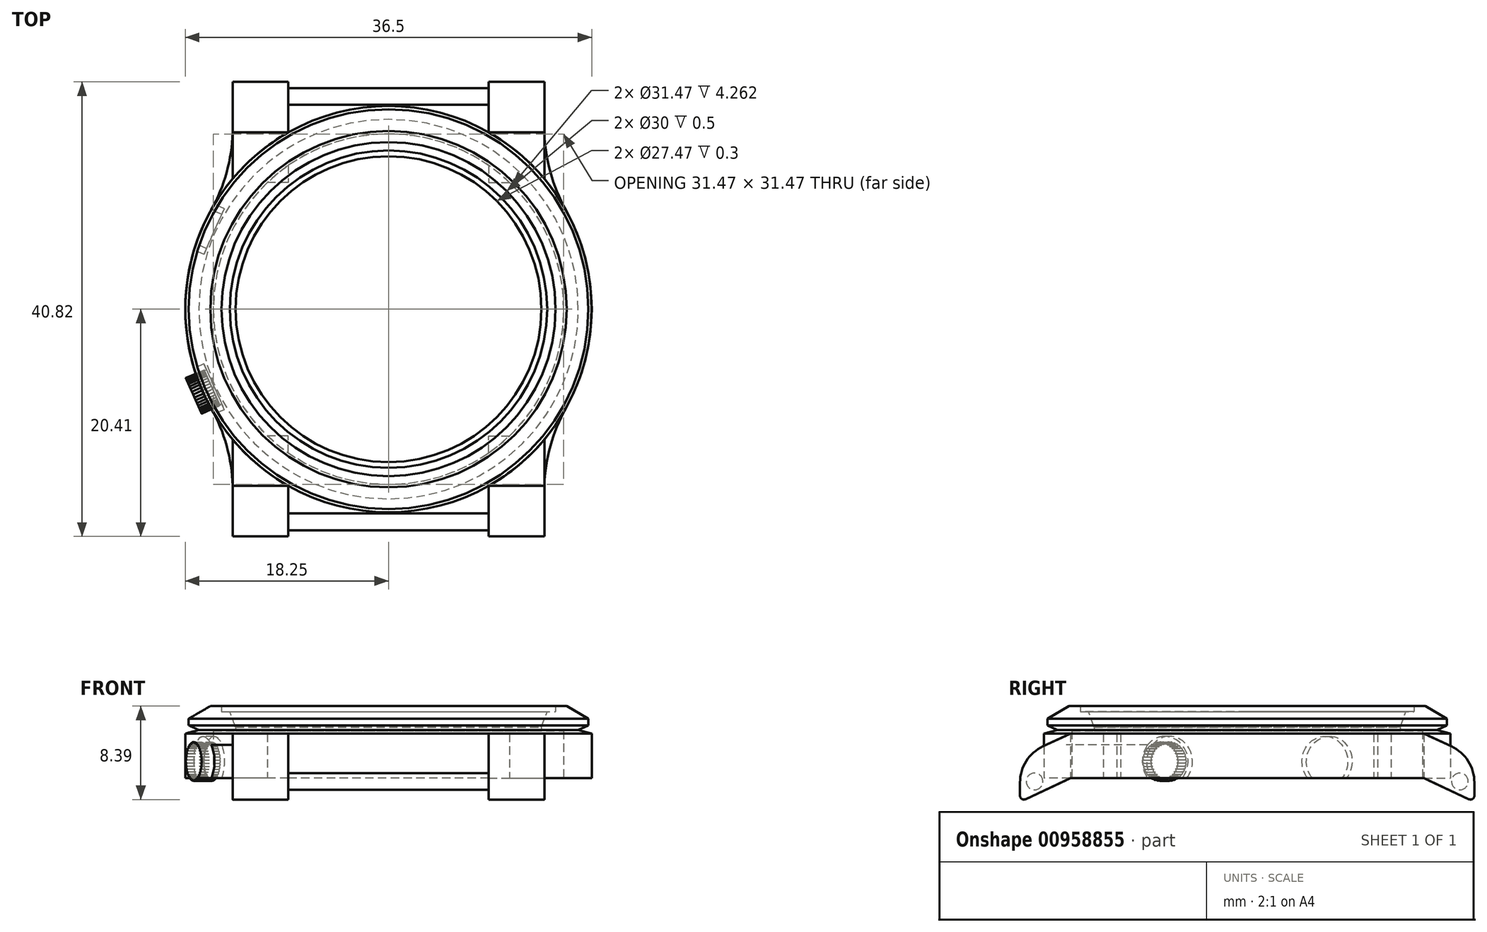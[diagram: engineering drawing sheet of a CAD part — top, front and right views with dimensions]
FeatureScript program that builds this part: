
annotation { "Feature Type Name" : "Feature", "Feature Type Description" : "" }
export const myFeature = defineFeature(function(context is Context, id is Id, definition is map)
    precondition{}
    {
        {
            var Q0;
            Q0=qCreatedBy(makeId("Right.planeOp"),FACE);
            var sketch = newSketch(context, id + "F0", { "sketchPlane" : qUnion([Q0])});
            skLineSegment(sketch, "E0", {"start": v(0, 0) * mm, "end": v(18.25, 0) * mm});
            skLineSegment(sketch, "E1", {"start": v(18.25, 0) * mm, "end": v(18.25, 4) * mm});
            skLineSegment(sketch, "E2", {"start": v(18.25, 4) * mm, "end": v(17.04, 4.32) * mm});
            skLineSegment(sketch, "E3", {"start": v(17.04, 4.32) * mm, "end": v(17.95, 4.75) * mm});
            skLineSegment(sketch, "E4", {"start": v(17.95, 4.75) * mm, "end": v(17.95, 5.35) * mm});
            skLineSegment(sketch, "E5", {"start": v(17.95, 5.35) * mm, "end": v(16, 6.47) * mm});
            skLineSegment(sketch, "E6", {"start": v(15, 5.97) * mm, "end": v(14.25, 5.97) * mm});
            skLineSegment(sketch, "E7", {"start": v(14.25, 5.97) * mm, "end": v(13.74, 4.56) * mm});
            skLineSegment(sketch, "E8", {"start": v(13.74, 4.56) * mm, "end": v(13.74, 4.26) * mm});
            skLineSegment(sketch, "E9", {"start": v(0, 0) * mm, "end": v(0, 9.09) * mm, "construction": true});
            skLineSegment(sketch, "E10", {"start": v(16, 6.47) * mm, "end": v(15, 6.47) * mm});
            skLineSegment(sketch, "E11", {"start": v(15, 6.47) * mm, "end": v(15, 5.97) * mm});
            skLineSegment(sketch, "E12", {"start": v(13.74, 4.26) * mm, "end": v(15.74, 4.26) * mm});
            skLineSegment(sketch, "E13", {"start": v(15.74, 4.26) * mm, "end": v(15.74, 0) * mm});
            skSolve(sketch);
        }
        {
            var Q0;
            Q0=qSketchRegion(id+"F0",true);
            var Q1;
            Q1=sQuery(id+"F0.wireOp",EDGE,"E9");
            revolve(context, id + "F1", {"entities" : qUnion([Q0]), "axis" : qUnion([Q1]), "revolveType" : RevolveType.FULL});
        }
        {
            var Q0;
            Q0=makeQuery(id+"F1.opRevolve","SWEPT_FACE",FACE,{"disambiguationData":[OSD([sQuery(id+"F0.wireOp",EDGE,"E0")])]});
            var sketch = newSketch(context, id + "F2", { "sketchPlane" : qUnion([Q0])});
            skLineSegment(sketch, "E14", {"start": v(-9, -15.88) * mm, "end": v(9, -15.88) * mm});
            skSolve(sketch);
        }
        {
            var Q0;
            Q0=qCreatedBy(makeId("Front.planeOp"),FACE);
            var Q1;
            Q1=sQuery(id+"F2.wireOp",VERTEX,"E14.start");
            cPlane(context, id + "F3", {"entities" : qUnion([Q0, Q1]), "cplaneType" : CPlaneType.PLANE_POINT, "offset" : 150 * mm, "width" : 150 * mm, "height" : 150 * mm});
        }
        {
            var Q0;
            Q0=qCreatedBy(id+"F3.planeOp",FACE);
            var sketch = newSketch(context, id + "F4", { "sketchPlane" : qUnion([Q0])});
            skLineSegment(sketch, "E15.bottom", {"start": v(-9, 0) * mm, "end": v(-14, 0) * mm});
            skLineSegment(sketch, "E15.top", {"start": v(-9, 4) * mm, "end": v(-14, 4) * mm});
            skLineSegment(sketch, "E15.left", {"start": v(-9, 0) * mm, "end": v(-9, 4) * mm});
            skLineSegment(sketch, "E15.right", {"start": v(-14, 0) * mm, "end": v(-14, 4) * mm});
            skSolve(sketch);
        }
        {
            var Q0;
            Q0=qCreatedBy(makeId("Top.planeOp"),FACE);
            var sketch = newSketch(context, id + "F5", { "sketchPlane" : qUnion([Q0])});
            skLineSegment(sketch, "E16", {"start": v(-11.51, 15.88) * mm, "end": v(-11.51, 11.38) * mm});
            skSolve(sketch);
        }
        {
            var Q0;
            Q0=sQuery(id+"F4.wireOp",EDGE,"E15.bottom");
            cPlane(context, id + "F6", {"entities" : qUnion([Q0]), "cplaneType" : CPlaneType.LINE_ANGLE, "offset" : 150 * mm, "angle" : 115 * degree, "width" : 150 * mm, "height" : 150 * mm});
        }
        {
            var Q0;
            Q0=qCreatedBy(id+"F6.planeOp",FACE);
            var sketch = newSketch(context, id + "F7", { "sketchPlane" : qUnion([Q0])});
            skLineSegment(sketch, "E17", {"start": v(-11.51, 14.39) * mm, "end": v(-11.51, 19.39) * mm});
            skSolve(sketch);
        }
        {
            var Q0;
            Q0=qSketchRegion(id+"F4",true);
            var Q1;
            Q1=sQuery(id+"F7.wireOp",EDGE,"E17");
            sweep(context, id + "F8", {"profiles" : qUnion([Q0]), "path" : qUnion([Q1])});
        }
        {
            var Q0;
            Q0=qSketchRegion(id+"F4",true);
            var Q1;
            Q1=qConstructionFilter(qBodyType(qCreatedBy(id+"F5",EDGE),BodyType.WIRE),ConstructionObject.NO);
            var Q2;
            Q2=qConstructionFilter(qBodyType(qCreatedBy(id+"F5",EDGE),BodyType.WIRE),ConstructionObject.NO);
            sweep(context, id + "F9", {"profiles" : qUnion([Q0]), "path" : qUnion([Q1, Q2])});
        }
        {
            var Q0;
            Q0=makeQuery(id+"F8.opSweep","CAP_EDGE",EDGE,{"disambiguationData":[OSD([sQuery(id+"F4.wireOp",EDGE,"E15.top"),sQuery(id+"F7.wireOp",VERTEX,"E17.end")])],"isStart":false});
            fillet(context, id + "F10", {"entities" : qUnion([Q0]), "radius" : 3.59 * mm, "tangentPropagation" : true, "allowEdgeOverflow" : false});
        }
        {
            var Q0;
            Q0=makeQuery(id+"F8.opSweep","CAP_EDGE",EDGE,{"disambiguationData":[OSD([sQuery(id+"F4.wireOp",EDGE,"E15.bottom"),sQuery(id+"F7.wireOp",VERTEX,"E17.end")])],"isStart":false});
            fillet(context, id + "F11", {"entities" : qUnion([Q0]), "radius" : 0.34 * mm, "tangentPropagation" : true, "allowEdgeOverflow" : false});
        }
        {
            var Q0;
            Q0=makeQuery(id+"F8.opSweep","SWEPT_BODY",BODY,{"disambiguationData":[OSD([sQuery(id+"F4.wireOp",EDGE,"E15.bottom"),sQuery(id+"F4.wireOp",EDGE,"E15.top"),sQuery(id+"F4.wireOp",EDGE,"E15.left"),sQuery(id+"F4.wireOp",EDGE,"E15.right"),sQuery(id+"F7.wireOp",EDGE,"E17")])]});
            var Q1;
            Q1=makeQuery(id+"F9.opSweep","SWEPT_BODY",BODY,{"disambiguationData":[OSD([sQuery(id+"F4.wireOp",EDGE,"E15.bottom"),sQuery(id+"F4.wireOp",EDGE,"E15.top"),sQuery(id+"F4.wireOp",EDGE,"E15.left"),sQuery(id+"F4.wireOp",EDGE,"E15.right"),sQuery(id+"F5.wireOp",EDGE,"E16")])]});
            var Q2;
            Q2=qCreatedBy(makeId("Right.planeOp"),FACE);
            mirror(context, id + "F12", {"entities" : qUnion([Q0, Q1]), "mirrorPlane" : qUnion([Q2])});
        }
        {
            var Q0;
            Q0=makeQuery(id+"F12.opPattern","COPY",BODY,{"derivedFrom":makeQuery(id+"F8.opSweep","SWEPT_BODY",BODY,{"disambiguationData":[OSD([sQuery(id+"F4.wireOp",EDGE,"E15.bottom"),sQuery(id+"F4.wireOp",EDGE,"E15.top"),sQuery(id+"F4.wireOp",EDGE,"E15.left"),sQuery(id+"F4.wireOp",EDGE,"E15.right"),sQuery(id+"F7.wireOp",EDGE,"E17")])]}),"instanceName":"1"});
            var Q1;
            Q1=makeQuery(id+"F12.opPattern","COPY",BODY,{"derivedFrom":makeQuery(id+"F9.opSweep","SWEPT_BODY",BODY,{"disambiguationData":[OSD([sQuery(id+"F4.wireOp",EDGE,"E15.bottom"),sQuery(id+"F4.wireOp",EDGE,"E15.top"),sQuery(id+"F4.wireOp",EDGE,"E15.left"),sQuery(id+"F4.wireOp",EDGE,"E15.right"),sQuery(id+"F5.wireOp",EDGE,"E16")])]}),"instanceName":"1"});
            var Q2;
            Q2=makeQuery(id+"F9.opSweep","SWEPT_BODY",BODY,{"disambiguationData":[OSD([sQuery(id+"F4.wireOp",EDGE,"E15.bottom"),sQuery(id+"F4.wireOp",EDGE,"E15.top"),sQuery(id+"F4.wireOp",EDGE,"E15.left"),sQuery(id+"F4.wireOp",EDGE,"E15.right"),sQuery(id+"F5.wireOp",EDGE,"E16")])]});
            var Q3;
            Q3=makeQuery(id+"F8.opSweep","SWEPT_BODY",BODY,{"disambiguationData":[OSD([sQuery(id+"F4.wireOp",EDGE,"E15.bottom"),sQuery(id+"F4.wireOp",EDGE,"E15.top"),sQuery(id+"F4.wireOp",EDGE,"E15.left"),sQuery(id+"F4.wireOp",EDGE,"E15.right"),sQuery(id+"F7.wireOp",EDGE,"E17")])]});
            var Q4;
            Q4=qCreatedBy(makeId("Front.planeOp"),FACE);
            mirror(context, id + "F13", {"operationType" : NewBodyOperationType.ADD, "entities" : qUnion([Q0, Q1, Q2, Q3]), "mirrorPlane" : qUnion([Q4])});
        }
        {
            var Q0;
            Q0=sQuery(id+"F0.wireOp",EDGE,"E9");
            cPlane(context, id + "F14", {"entities" : qUnion([Q0]), "cplaneType" : CPlaneType.LINE_ANGLE, "offset" : 150 * mm, "angle" : 114 * degree, "width" : 150 * mm, "height" : 150 * mm});
        }
        {
            var Q0;
            Q0=qCreatedBy(id+"F14.planeOp",FACE);
            var sketch = newSketch(context, id + "F15", { "sketchPlane" : qUnion([Q0])});
            skLineSegment(sketch, "E18", {"start": v(18.15, 4) * mm, "end": v(18.15, 0) * mm});
            skLineSegment(sketch, "E19", {"start": v(18.15, 4) * mm, "end": v(20.15, 4) * mm, "construction": true});
            skLineSegment(sketch, "E20", {"start": v(18.15, 1.5) * mm, "end": v(19.95, 1.5) * mm, "construction": true});
            skSolve(sketch);
        }
        {
            var Q0;
            Q0=sQuery(id+"F15.wireOp",EDGE,"E18");
            cPlane(context, id + "F16", {"entities" : qUnion([Q0]), "cplaneType" : CPlaneType.LINE_ANGLE, "offset" : 150 * mm, "angle" : 156 * degree, "width" : 150 * mm, "height" : 150 * mm});
        }
        {
            var Q0;
            Q0=qCreatedBy(id+"F16.planeOp",FACE);
            var sketch = newSketch(context, id + "F17", { "sketchPlane" : qUnion([Q0])});
            skCircle(sketch, "E21", {"center": v(0, 1.5) * mm, "radius": 2.25 * mm});
            skSolve(sketch);
        }
        {
            var Q0;
            Q0=qSketchRegion(id+"F17",true);
            extrude(context, id + "F18", {"entities" : qUnion([Q0]), "operationType" : NewBodyOperationType.REMOVE, "depth" : 1 * mm, "hasSecondDirection" : true, "secondDirectionBound" : SecondDirectionBoundingType.THROUGH_ALL, "secondDirectionOppositeDirection" : true, "secondDirectionDepth" : 25 * mm});
        }
        {
            var Q0;
            Q0=qCreatedBy(id+"F16.planeOp",FACE);
            var sketch = newSketch(context, id + "F19", { "sketchPlane" : qUnion([Q0])});
            skCircle(sketch, "E22", {"center": v(0, 1.5) * mm, "radius": 1.75 * mm});
            skSolve(sketch);
        }
        {
            var Q0;
            Q0=qSketchRegion(id+"F19",true);
            extrude(context, id + "F20", {"entities" : qUnion([Q0]), "depth" : .8 * mm, "hasSecondDirection" : true, "secondDirectionOppositeDirection" : true, "secondDirectionDepth" : 1 * mm});
        }
        {
            var Q0;
            Q0=qCreatedBy(id+"F16.planeOp",FACE);
            var sketch = newSketch(context, id + "F21", { "sketchPlane" : qUnion([Q0])});
            skCircle(sketch, "E23", {"center": v(0, -0.12) * mm, "radius": 0.12 * mm});
            skPoint(sketch, "E23.first.point", {"position": v(0, -0.25) * mm});
            skPoint(sketch, "E23.second.point", {"position": v(0, 0) * mm});
            skPoint(sketch, "E23.third.point", {"position": v(0.12, -0.15) * mm});
            skCircle(sketch, "E24", {"center": v(-0.25, -0.1) * mm, "radius": 0.12 * mm});
            skPoint(sketch, "E24.first.point", {"position": v(-0.27, -0.23) * mm});
            skPoint(sketch, "E24.second.point", {"position": v(-0.24, 0.02) * mm});
            skPoint(sketch, "E24.third.point", {"position": v(-0.3, 0) * mm});
            skLineSegment(sketch, "E25", {"start": v(0, -0.25) * mm, "end": v(-0.14, -0.32) * mm});
            skLineSegment(sketch, "E26", {"start": v(-0.14, -0.32) * mm, "end": v(-0.27, -0.23) * mm});
            skSolve(sketch);
        }
        {
            var Q0;
            {var subQ1=sQuery(id+"F21.wireOp",EDGE,"E25");Q0=makeQuery(id+"F21.imprint","IMPRINT",FACE,{"disambiguationData":[TD([[makeQuery(id+"F21.imprint","IMPRINT",EDGE,{"derivedFrom":subQ1}),-1.0]])]});}
            extrude(context, id + "F22", {"entities" : qUnion([Q0]), "endBound" : BoundingType.UP_TO_NEXT, "oppositeDirection" : true, "depth" : 25 * mm, "hasSecondDirection" : true, "secondDirectionBound" : SecondDirectionBoundingType.THROUGH_ALL, "secondDirectionOppositeDirection" : false, "secondDirectionDepth" : 25 * mm});
        }
        {
            var Q0;
            Q0=makeQuery(id+"F22.opExtrude","SWEPT_BODY",BODY,{"disambiguationData":[OSD([sQuery(id+"F21.wireOp",EDGE,"E23"),sQuery(id+"F21.wireOp",EDGE,"E24"),sQuery(id+"F21.wireOp",EDGE,"E25"),sQuery(id+"F21.wireOp",EDGE,"E26")])]});
            var Q1;
            Q1=sQuery(id+"F15.wireOp",EDGE,"E20");
            circularPattern(context, id + "F23", {"operationType" : NewBodyOperationType.REMOVE, "entities" : qUnion([Q0]), "axis" : qUnion([Q1]), "angle" : 10 * degree, "instanceCount" : 37});
        }
        {
            var Q0;
            {var subQ0=sQuery(id+"F4.wireOp",EDGE,"E15.left");Q0=makeQuery(id+"F13.boolean.opBoolean","MERGE",FACE,{"disambiguationData":[OD(1.0)],"derivedFrom":[makeQuery(id+"F12.opPattern","COPY",FACE,{"derivedFrom":makeQuery(id+"F9.opSweep","SWEPT_FACE",FACE,{"disambiguationData":[OSD([subQ0,sQuery(id+"F5.wireOp",EDGE,"E16")])]}),"instanceName":"1"}),makeQuery(id+"F12.opPattern","COPY",FACE,{"derivedFrom":makeQuery(id+"F8.opSweep","SWEPT_FACE",FACE,{"disambiguationData":[OSD([subQ0,sQuery(id+"F7.wireOp",EDGE,"E17")])]}),"instanceName":"1"})]});}
            var sketch = newSketch(context, id + "F24", { "sketchPlane" : qUnion([Q0])});
            skCircle(sketch, "E27", {"center": v(-19.1, -0.3) * mm, "radius": 0.75 * mm});
            skSolve(sketch);
        }
        {
            var Q0;
            Q0=qSketchRegion(id+"F24",true);
            extrude(context, id + "F25", {"entities" : qUnion([Q0]), "operationType" : NewBodyOperationType.ADD, "endBound" : BoundingType.UP_TO_NEXT, "depth" : 25 * mm});
        }
        {
            var Q0;
            Q0=makeQuery(id+"F1.opRevolve","SWEPT_BODY",BODY,{"disambiguationData":[OSD([sQuery(id+"F0.wireOp",EDGE,"E0"),sQuery(id+"F0.wireOp",EDGE,"E1"),sQuery(id+"F0.wireOp",EDGE,"E2"),sQuery(id+"F0.wireOp",EDGE,"E3"),sQuery(id+"F0.wireOp",EDGE,"E4"),sQuery(id+"F0.wireOp",EDGE,"E5"),sQuery(id+"F0.wireOp",EDGE,"E6"),sQuery(id+"F0.wireOp",EDGE,"E7"),sQuery(id+"F0.wireOp",EDGE,"E8"),sQuery(id+"F0.wireOp",EDGE,"E10"),sQuery(id+"F0.wireOp",EDGE,"E11"),sQuery(id+"F0.wireOp",EDGE,"E12"),sQuery(id+"F0.wireOp",EDGE,"E13")])]});
            var Q1;
            Q1=qCreatedBy(makeId("Front.planeOp"),FACE);
            mirror(context, id + "F26", {"entities" : qUnion([Q0]), "mirrorPlane" : qUnion([Q1])});
        }
        {
            var Q0;
            {var subQ0=sQuery(id+"F4.wireOp",EDGE,"E15.right");Q0=makeQuery(id+"F13.boolean.opBoolean","INTERSECT",EDGE,{"derivedFrom":[makeQuery(id+"F1.opRevolve","SWEPT_FACE",FACE,{"disambiguationData":[OSD([sQuery(id+"F0.wireOp",EDGE,"E1")])]}),makeQuery(id+"F13.opPattern","COPY",FACE,{"derivedFrom":makeQuery(id+"F12.opPattern","COPY",FACE,{"derivedFrom":makeQuery(id+"F9.opSweep","SWEPT_FACE",FACE,{"disambiguationData":[OSD([subQ0,sQuery(id+"F5.wireOp",EDGE,"E16")])]}),"instanceName":"1"}),"instanceName":"1"}),makeQuery(id+"F13.opPattern","COPY",FACE,{"derivedFrom":makeQuery(id+"F12.opPattern","COPY",FACE,{"derivedFrom":makeQuery(id+"F8.opSweep","SWEPT_FACE",FACE,{"disambiguationData":[OSD([subQ0,sQuery(id+"F7.wireOp",EDGE,"E17")])]}),"instanceName":"1"}),"instanceName":"1"})]});}
            var Q1;
            {var subQ0=sQuery(id+"F4.wireOp",EDGE,"E15.right");Q1=makeQuery(id+"F13.boolean.opBoolean","INTERSECT",EDGE,{"derivedFrom":[makeQuery(id+"F1.opRevolve","SWEPT_FACE",FACE,{"disambiguationData":[OSD([sQuery(id+"F0.wireOp",EDGE,"E1")])]}),makeQuery(id+"F12.opPattern","COPY",FACE,{"derivedFrom":makeQuery(id+"F9.opSweep","SWEPT_FACE",FACE,{"disambiguationData":[OSD([subQ0,sQuery(id+"F5.wireOp",EDGE,"E16")])]}),"instanceName":"1"}),makeQuery(id+"F12.opPattern","COPY",FACE,{"derivedFrom":makeQuery(id+"F8.opSweep","SWEPT_FACE",FACE,{"disambiguationData":[OSD([subQ0,sQuery(id+"F7.wireOp",EDGE,"E17")])]}),"instanceName":"1"})]});}
            var Q2;
            {var subQ0=sQuery(id+"F4.wireOp",EDGE,"E15.right");Q2=makeQuery(id+"F13.boolean.opBoolean","INTERSECT",EDGE,{"derivedFrom":[makeQuery(id+"F1.opRevolve","SWEPT_FACE",FACE,{"disambiguationData":[OSD([sQuery(id+"F0.wireOp",EDGE,"E1")])]}),makeQuery(id+"F9.opSweep","SWEPT_FACE",FACE,{"disambiguationData":[OSD([subQ0,sQuery(id+"F5.wireOp",EDGE,"E16")])]}),makeQuery(id+"F8.opSweep","SWEPT_FACE",FACE,{"disambiguationData":[OSD([subQ0,sQuery(id+"F7.wireOp",EDGE,"E17")])]})]});}
            var Q3;
            {var subQ0=sQuery(id+"F4.wireOp",EDGE,"E15.right");Q3=makeQuery(id+"F13.boolean.opBoolean","INTERSECT",EDGE,{"derivedFrom":[makeQuery(id+"F1.opRevolve","SWEPT_FACE",FACE,{"disambiguationData":[OSD([sQuery(id+"F0.wireOp",EDGE,"E1")])]}),makeQuery(id+"F13.opPattern","COPY",FACE,{"derivedFrom":makeQuery(id+"F9.opSweep","SWEPT_FACE",FACE,{"disambiguationData":[OSD([subQ0,sQuery(id+"F5.wireOp",EDGE,"E16")])]}),"instanceName":"1"}),makeQuery(id+"F13.opPattern","COPY",FACE,{"derivedFrom":makeQuery(id+"F8.opSweep","SWEPT_FACE",FACE,{"disambiguationData":[OSD([subQ0,sQuery(id+"F7.wireOp",EDGE,"E17")])]}),"instanceName":"1"})]});}
            fillet(context, id + "F27", {"entities" : qUnion([Q0, Q1, Q2, Q3]), "radius" : 15 * mm, "tangentPropagation" : true, "allowEdgeOverflow" : false});
        }
    });
